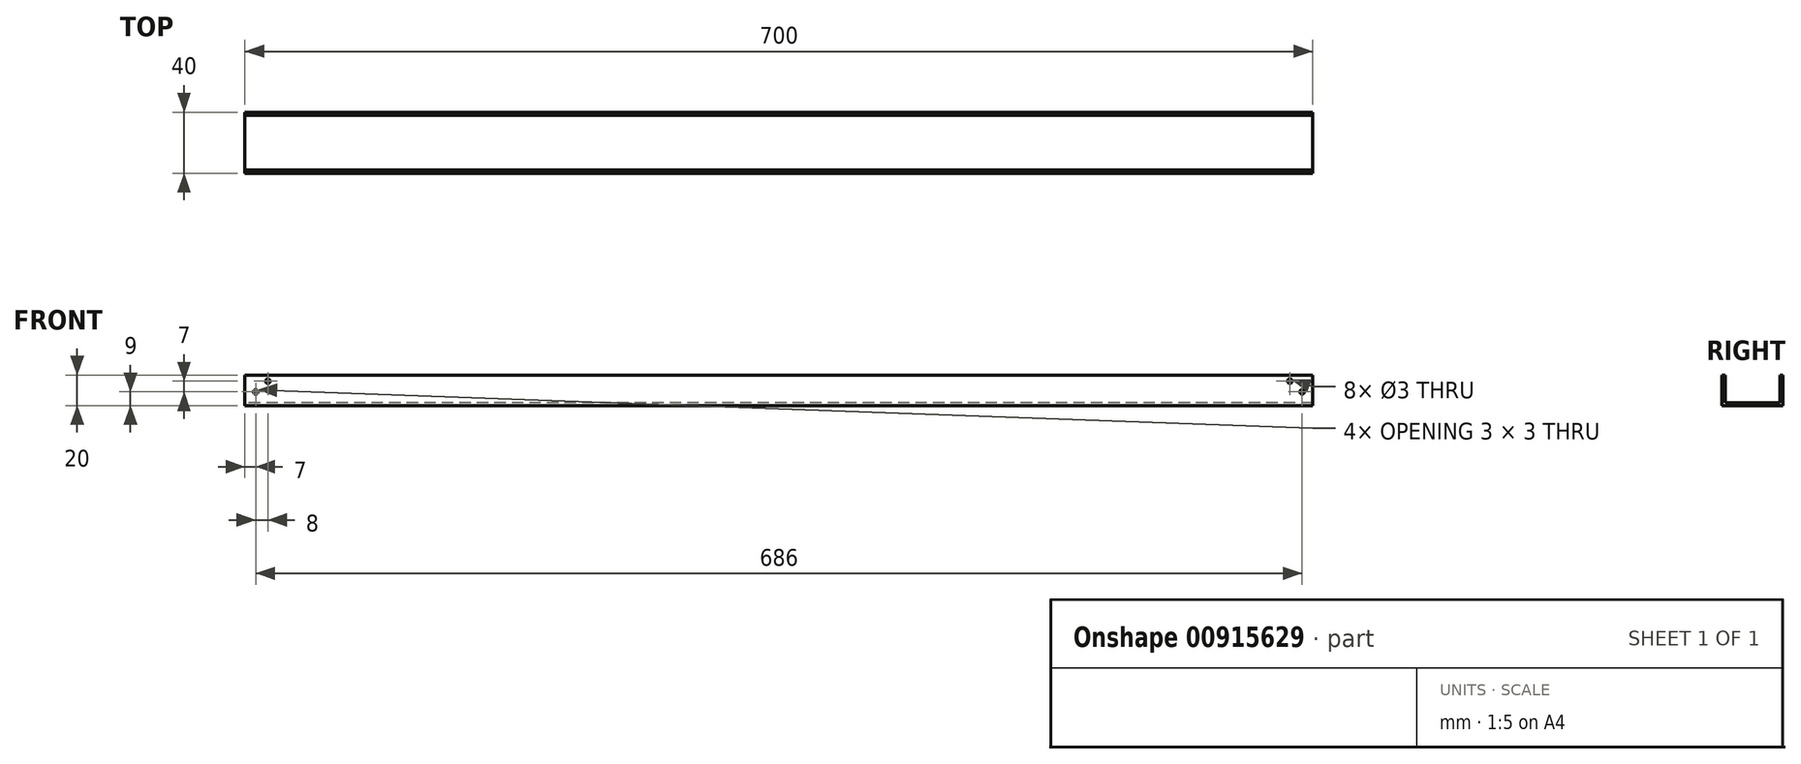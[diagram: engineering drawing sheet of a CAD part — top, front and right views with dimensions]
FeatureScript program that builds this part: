
annotation { "Feature Type Name" : "Feature", "Feature Type Description" : "" }
export const myFeature = defineFeature(function(context is Context, id is Id, definition is map)
    precondition{}
    {
        {
            var Q0;
            Q0=qCreatedBy(makeId("Right.planeOp"),FACE);
            var sketch = newSketch(context, id + "F0", { "sketchPlane" : qUnion([Q0])});
            skLineSegment(sketch, "E0.bottom", {"start": v(-20, 0) * mm, "end": v(20, 0) * mm});
            skLineSegment(sketch, "E0.top", {"start": v(-20, 20) * mm, "end": v(20, 20) * mm});
            skLineSegment(sketch, "E0.left", {"start": v(-20, 0) * mm, "end": v(-20, 20) * mm});
            skLineSegment(sketch, "E0.right", {"start": v(20, 0) * mm, "end": v(20, 20) * mm});
            skPoint(sketch, "E0.middle", {"position": v(0, 10) * mm});
            skLineSegment(sketch, "E1.bottom", {"start": v(-18, 20) * mm, "end": v(18, 20) * mm});
            skLineSegment(sketch, "E1.top", {"start": v(-18, 2) * mm, "end": v(18, 2) * mm});
            skLineSegment(sketch, "E1.left", {"start": v(-18, 20) * mm, "end": v(-18, 2) * mm});
            skLineSegment(sketch, "E1.right", {"start": v(18, 20) * mm, "end": v(18, 2) * mm});
            skPoint(sketch, "E1.middle", {"position": v(0, 11) * mm});
            skSolve(sketch);
        }
        {
            var Q0;
            Q0=makeQuery(id+"F0.imprint","IMPRINT",FACE,{"disambiguationData":[TD([[makeQuery(id+"F0.imprint","IMPRINT",EDGE,{"derivedFrom":sQuery(id+"F0.wireOp",EDGE,"E0.bottom")}),1.0]])]});
            extrude(context, id + "F1", {"entities" : qUnion([Q0]), "depth" : 350 * mm, "offsetDistance" : 25 * mm, "hasSecondDirection" : true, "secondDirectionOppositeDirection" : true, "secondDirectionDepth" : 350 * mm});
        }
        {
            var Q0;
            Q0=makeQuery(id+"F1.opExtrude","SWEPT_FACE",FACE,{"disambiguationData":[OSD([sQuery(id+"F0.wireOp",EDGE,"E1.left")])]});
            var sketch = newSketch(context, id + "F2", { "sketchPlane" : qUnion([Q0])});
            skLineSegment(sketch, "E2.bottom", {"start": v(350, 2) * mm, "end": v(343, 2) * mm});
            skLineSegment(sketch, "E2.top", {"start": v(350, 9) * mm, "end": v(343, 9) * mm});
            skLineSegment(sketch, "E2.left", {"start": v(350, 2) * mm, "end": v(350, 9) * mm});
            skLineSegment(sketch, "E2.right", {"start": v(343, 2) * mm, "end": v(343, 9) * mm});
            skLineSegment(sketch, "E3.bottom", {"start": v(-350, 2) * mm, "end": v(-343, 2) * mm});
            skLineSegment(sketch, "E3.top", {"start": v(-350, 9) * mm, "end": v(-343, 9) * mm});
            skLineSegment(sketch, "E3.left", {"start": v(-350, 2) * mm, "end": v(-350, 9) * mm});
            skLineSegment(sketch, "E3.right", {"start": v(-343, 2) * mm, "end": v(-343, 9) * mm});
            skLineSegment(sketch, "E4.top", {"start": v(350, 16) * mm, "end": v(343, 16) * mm});
            skLineSegment(sketch, "E4.left", {"start": v(350, 9) * mm, "end": v(350, 16) * mm});
            skLineSegment(sketch, "E4.right", {"start": v(343, 9) * mm, "end": v(343, 16) * mm});
            skLineSegment(sketch, "E5.top", {"start": v(-350, 16) * mm, "end": v(-343, 16) * mm});
            skLineSegment(sketch, "E5.left", {"start": v(-350, 9) * mm, "end": v(-350, 16) * mm});
            skLineSegment(sketch, "E5.right", {"start": v(-343, 9) * mm, "end": v(-343, 16) * mm});
            skLineSegment(sketch, "E6", {"start": v(-343, 16) * mm, "end": v(-335, 16) * mm});
            skLineSegment(sketch, "E7", {"start": v(343, 16) * mm, "end": v(335, 16) * mm});
            skSolve(sketch);
        }
        {
            var Q0;
            Q0=sQuery(id+"F2.wireOp",VERTEX,"E3.top.end");
            var Q1;
            Q1=sQuery(id+"F2.wireOp",VERTEX,"E2.top.end");
            var Q2;
            Q2=sQuery(id+"F2.wireOp",VERTEX,"E7.end");
            var Q3;
            Q3=sQuery(id+"F2.wireOp",VERTEX,"E6.end");
            var Q4;
            Q4=makeQuery(id+"F1.opExtrude","SWEPT_BODY",BODY,{"disambiguationData":[OSD([sQuery(id+"F0.wireOp",EDGE,"E0.bottom"),sQuery(id+"F0.wireOp",EDGE,"E0.top"),sQuery(id+"F0.wireOp",EDGE,"E0.left"),sQuery(id+"F0.wireOp",EDGE,"E0.right"),sQuery(id+"F0.wireOp",EDGE,"E1.top"),sQuery(id+"F0.wireOp",EDGE,"E1.left"),sQuery(id+"F0.wireOp",EDGE,"E1.right")])]});
            hole(context, id + "F3", {"style" : HoleStyle.SIMPLE, "endStyle" : HoleEndStyle.BLIND, "holeDiameter" : 3 * mm, "majorDiameter" : 5 * mm, "holeDepth" : 50 * mm, "isTappedThrough" : true, "tappedDepth" : 12 * mm, "tapClearance" : 3, "locations" : qUnion([Q0, Q1, Q2, Q3]), "scope" : qUnion([Q4])});
        }
        {
            var Q0;
            Q0=sQuery(id+"F2.wireOp",VERTEX,"E3.top.end");
            var Q1;
            Q1=sQuery(id+"F2.wireOp",VERTEX,"E2.top.end");
            var Q2;
            Q2=sQuery(id+"F2.wireOp",VERTEX,"E6.end");
            var Q3;
            Q3=sQuery(id+"F2.wireOp",VERTEX,"E7.end");
            var Q4;
            Q4=makeQuery(id+"F1.opExtrude","SWEPT_BODY",BODY,{"disambiguationData":[OSD([sQuery(id+"F0.wireOp",EDGE,"E0.bottom"),sQuery(id+"F0.wireOp",EDGE,"E0.top"),sQuery(id+"F0.wireOp",EDGE,"E0.left"),sQuery(id+"F0.wireOp",EDGE,"E0.right"),sQuery(id+"F0.wireOp",EDGE,"E1.top"),sQuery(id+"F0.wireOp",EDGE,"E1.left"),sQuery(id+"F0.wireOp",EDGE,"E1.right")])]});
            hole(context, id + "F4", {"style" : HoleStyle.SIMPLE, "endStyle" : HoleEndStyle.BLIND, "oppositeDirection" : true, "holeDiameter" : 3 * mm, "majorDiameter" : 5 * mm, "holeDepth" : 50 * mm, "isTappedThrough" : true, "tappedDepth" : 12 * mm, "tapClearance" : 3, "locations" : qUnion([Q0, Q1, Q2, Q3]), "scope" : qUnion([Q4])});
        }
    });
